# Revit family: Faucet-Lavatory-Grohe-Essence_New-20297_Series
name_source: partatom
category: Plumbing Fixtures
revit_build: Autodesk Revit 2018 (Build: 20170223_1515(x64)
units: mm (PartAtom-declared; Revit-internal decimal feet)

## family parameters
Always vertical = No
Cut with Voids When Loaded = No
OmniClass Number = 23.45.55.17
OmniClass Title = Mixing Faucets
Part Type = Normal
Room Calculation Point = No
Round Connector Dimension = Use Diameter
Shared = Yes
Work Plane-Based = Yes

## types (5) — shared parameters
ADA Compliant = Yes
Assembly Code = D2020300
CW Connection = Yes
CWFU = 1.5
Cold Water Connection Diameter = 1 1/4"
Default Elevation = 0"
Description = 8-inch Widespread 2-Handle M-Size Bathroom Faucet 1.2 GPM
Flow Rate = 1.2 gpm (4.56 L/min)
HW Connection = Yes
HWFU = 1.5
Height = 7 5/8"
Hot Water Connection Diameter = 1"
Installation Type = Deck-Mounted
Length = 4 1/2"
Manufacturer = Grohe
Max. Working Pressure = 145 psi
Price = Prices may vary. Please consult Manufacturer Representative for most up-to-date price list.
Product Documentation Link = https://americanstandard.box.com
Product Page URL = https://www.grohe.us
Revised Date = 26/05/2021
URL = https://www.grohe.us
Vent Connection = No
Warranty Documentation Link = https://cdn.cloud.grohe.com
Warranty Information = Limited Lifetime Warranty
Waste Connection = No
cUPC Compliant = Yes
zero-valued in all types: WFU

## per-type parameters (varying)
| type | Finish | Material |
| 20297GNA | Brass-Grohe-GNA-Brushed Cool Sunrise | Brass-Grohe-GNA-Brushed Cool Sunrise |
| 2029700A | Brass-Grohe-00A-StarLight Chrome | Brass-Grohe-00A-StarLight Chrome |
| 20297A0A | Brass-Grohe-A0A-Hard Graphite | Brass-Grohe-A0A-Hard Graphite |
| 20297ENA | Brass-Grohe-ENA-Brushed Nickel Infinity Finish | Brass-Grohe-ENA-Brushed Nickel Infinity Finish |
| 20297BEA | Brass-Grohe-BEA-Polished Nickel Infinity Finish | Brass-Grohe-BEA-Polished Nickel Infinity Finish |

note: column(s) folded — value = type name in every type: Model

## geometry (parser evidence)
native form markers: Sweep x2
no freeform markers — native parametric forms only
